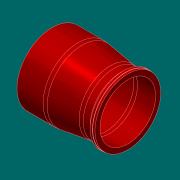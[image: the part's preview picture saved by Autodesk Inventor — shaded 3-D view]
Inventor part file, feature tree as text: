
AUTODESK INVENTOR PART (.ipt)
format: ipt  version: 2017.3 (Build 213256000, 256)  size: 248,832 bytes
history: native  units: in
note: dims shown in document units (in); Inventor stores cm internally (conversion verified against a paired STEP export)
features: sketch x4, extrude x3, chamfer x2, revolve x1, fillet x1
ambient origin geometry x8: Origin, YZ Plane, XZ Plane, XY Plane, X Axis, Y Axis, Z Axis, Center Point
bodies: Solid1 (feature_tree)
feature tree (11):
  revolve  "Revolution1"  [1 undecoded]
  extrude  "Extrusion1"  Depth=24.5in
  extrude  "Extrusion2"  Depth=12.0in
  chamfer  "Chamfer2"  Distance=12.0in
  extrude  "Extrusion3"  Depth=1.0in
  fillet  "Fillet1"  Radius=1.25in
  chamfer  "Chamfer1"  Distance=8.0in
  sketch  "Sketch1"  dims[d0=33.3346in d1=28.5in]
  sketch  "Sketch2"  dims[d2=1.25in d3=24.5in]
  sketch  "Sketch3"  dims[d4=12.0in d5=12.0in]
  sketch  "Sketch4"  dims[d6=12.0in d7=12.0in d8=1.5in d9=1.25in d10=8.0in d12=0.0559in d13=90.0deg d14=30.0in d15=0.5in d16=0.0in d17=29.25in d18=2.0in d19=0.0in d20=0.0312in d21=0.0312in d22=0.125in d23=45.0deg d24=1.125in d25=0.125in d26=45.0deg d27=28.98in d28=1.0in d29=0.0in]
note: 1 required parameter value undecoded (feature->parameter linkage not recoverable at this tier; creation-order binding heuristic only, values carry confidence <= 0.55)
